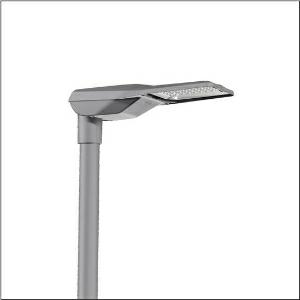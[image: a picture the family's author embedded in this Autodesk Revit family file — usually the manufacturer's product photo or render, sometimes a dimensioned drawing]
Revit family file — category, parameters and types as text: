
# Revit family: streetlight_sl_21_mini___st1_5a_5xe6p33a08gb_8a0c
name_source: partatom
category: Lighting Fixtures
units: mm (PartAtom-declared; Revit-internal decimal feet)

## family parameters
Cut with Voids When Loaded = No
Host = Face
Light Source = No
Part Type = Normal
Room Calculation Point = No
Round Connector Dimension = Use Diameter
Shared = No

## types (1)
- --- (1 x LED, 5840 lm, 40.4 W, 3000K)
    Apparent Load = 40 VA
    CIE Flux Codes = 22 53 95 100 100
    Color Rendering = 70
    Color Temperature = 3000K
    Default Elevation = 1800 mm
    Description = Streetlight SL 21 mini, mast luminaire, primary light control with lens, of PMMA, primary optical cover: cover, of toughened safety glass, transparent, light distribution: ST1.5a, light emission: direct distribution, primary light characteristic: asymmetric, installation type: post-top, side-entry, LED, 3G 1.5mm², High Power LED, rated luminous flux: 5.840lm, luminous efficacy: 145lm/W, light colour: 730, colour temperature: 3000K, control gear: Easy, control: overheat protection, constant luminous flux control, time-dependent luminous flux control, flexible luminous flux parameterisation, mains connection: 230..240V, AC, 50/60Hz, connection cable pre-assembled, cable length: 6,5m, wiring characteristics: H07RN-F, start of lifetime: 40W, end of service life: 41W, reduction: 19W, luminaire housing, of diecast aluminium, powder-coated, Siteco® metallic grey (DB 702S), corrosivity category C5 mid according to DIN EN ISO 12944, please order mast flange separately, inclination adjustable: 0°, 5°, 10°, 15°, sealing non-destructively replaceable, multi-level sealing system, length: 628mm, width: 235mm, height: 110mm, mast flange for spigot size: 42mm (side-entry): 5XC10008XM4, 60/48mm (side-entry/post-top): 5XC10108XM2, 76/60mm (side-entry/post-top): 5XC10108XM1, mounting height: 4..8m, protection rating (complete): IP66, insulation class (complete): insulation class II (safety insulation), certification: CE, ENEC, ENEC+, VDE, impact resistance: IK10, permissible operating ambient temperature for outdoor applications: -40..+50°C, standard-compliant lighting for roads and squares, packaging unit: 1 piece

Light Distribution: ST1.5a
    Height = 110 mm
    Lamp = 1 x LED
    Lamp Light Flux = 5840 lm
    Lamp Power = 40.4 W
    Lamp count = 1
    Length = 625 mm
    Luminous efficacy = 145 lm/W
    Manufacturer = Siteco
    ModVariant = No
    Model = 5XE6P33A08GB
    Number of Poles = 1
    OnlyDefault = Yes
    Power Factor = 1
    Product Name = Streetlight SL 21 mini | ST1.5a
    Product group = mast luminaire | pylon top
    ProductGroupID = 6100
    Protection Class = Protection class II
    Protection Degree = IP 66
    RLX_Detail_Level = 1
    RLX_Emergency_Light_Flux = 0 lm
    RLX_Emergency_Type = 0
    RLX_Emergency_Type_DB = No
    RlxData = <blob elided: 29445 chars, md5=0066418c>
    Socket = socket
    Standby Power = 0 W
    System Light Flux = 5840 lm
    System Power = 40 W
    Type Comments = factory setting: luminous flux: 100 % | Output Level: 100 % | 812 mA
    Type Image = l_1003519.jpg
    URL = http://relux.com
    VarID = @adj_196893
    Voltage = 0 V
    Weight = 0.00 kg
    Width = 234 mm

## geometry (parser evidence)
native form markers: Blend x4, Sweep x11
no freeform markers — native parametric forms only
